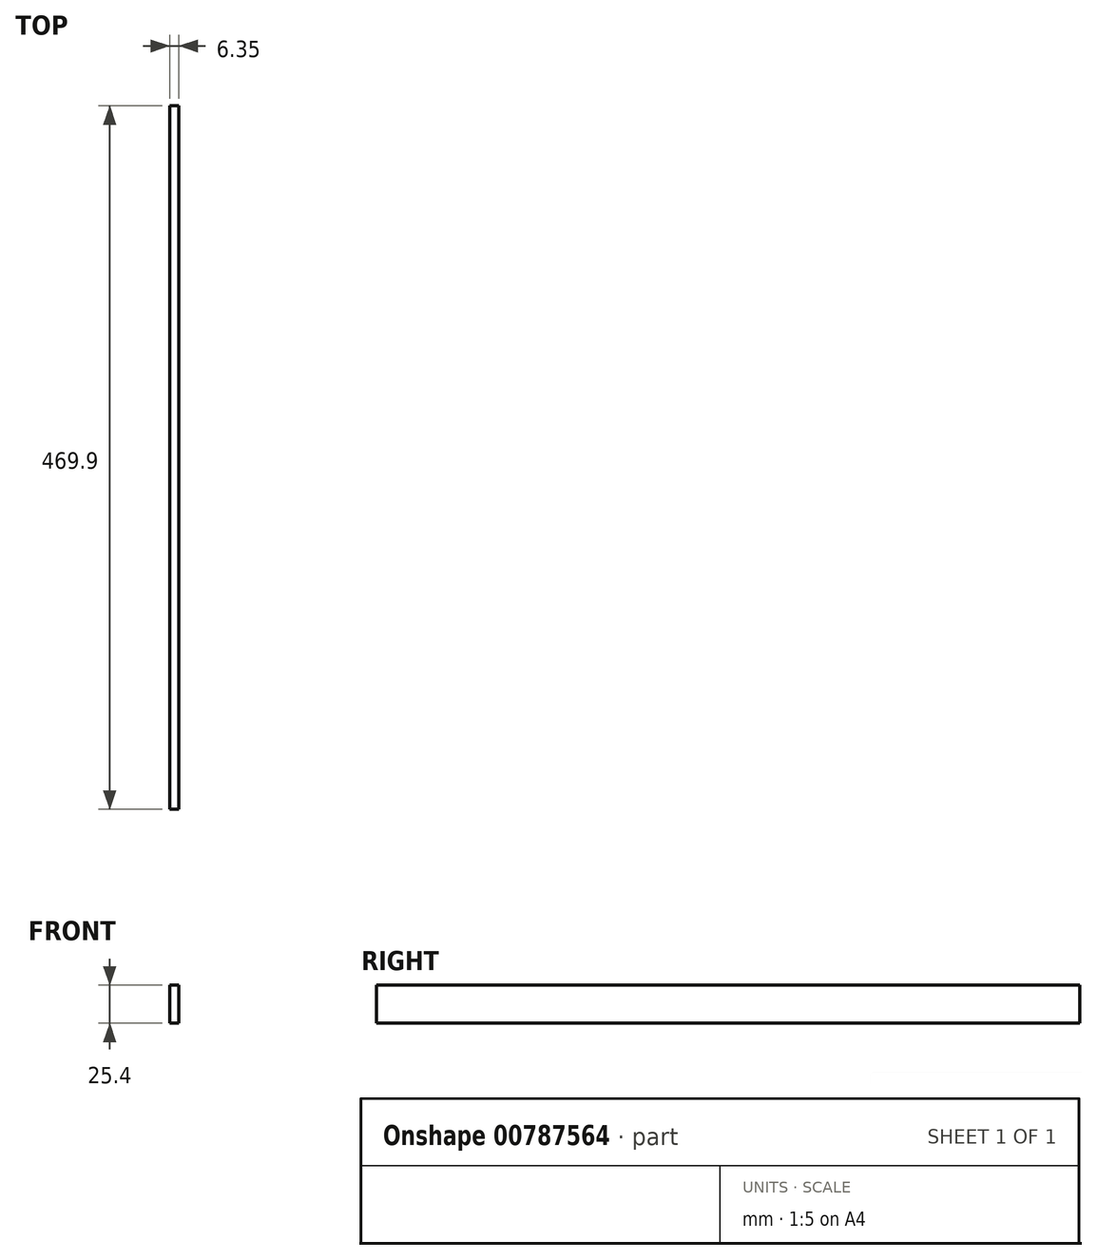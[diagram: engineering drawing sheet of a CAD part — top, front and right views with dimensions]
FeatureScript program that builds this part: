
annotation { "Feature Type Name" : "Feature", "Feature Type Description" : "" }
export const myFeature = defineFeature(function(context is Context, id is Id, definition is map)
    precondition{}
    {
        {
            var Q0;
            Q0=qCreatedBy(makeId("Right.planeOp"),FACE);
            var sketch = newSketch(context, id + "F0", { "sketchPlane" : qUnion([Q0])});
            skLineSegment(sketch, "E0.bottom", {"start": v(234.95, -12.7) * mm, "end": v(-234.95, -12.7) * mm});
            skLineSegment(sketch, "E0.top", {"start": v(234.95, 12.7) * mm, "end": v(-234.95, 12.7) * mm});
            skLineSegment(sketch, "E0.left", {"start": v(234.95, -12.7) * mm, "end": v(234.95, 12.7) * mm});
            skLineSegment(sketch, "E0.right", {"start": v(-234.95, -12.7) * mm, "end": v(-234.95, 12.7) * mm});
            skPoint(sketch, "E0.middle", {"position": v(0, 0) * mm});
            skSolve(sketch);
        }
        {
            var Q0;
            Q0=qSketchRegion(id+"F0",true);
            extrude(context, id + "F1", {"entities" : qUnion([Q0]), "depth" : 6.35 * mm, "offsetDistance" : 25.4 * mm});
        }
    });
